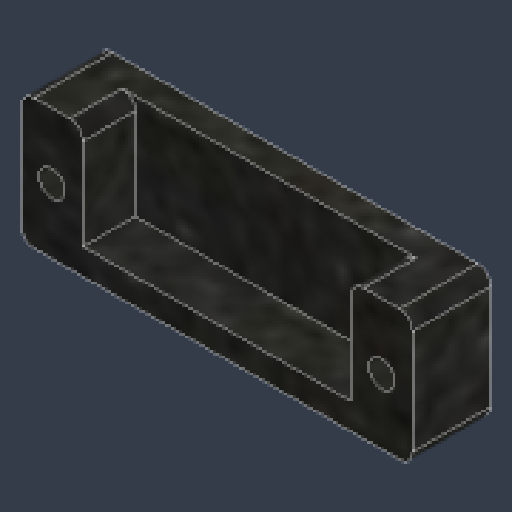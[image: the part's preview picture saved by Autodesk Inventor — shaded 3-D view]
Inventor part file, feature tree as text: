
AUTODESK INVENTOR PART (.ipt)
format: ipt  version: 2023.4 (Build 274418000, 418)  size: 148,480 bytes
history: native  units: mm
features: sketch x3, extrude x2, hole x1, fillet x1
ambient origin geometry x8: Origin, YZ Plane, XZ Plane, XY Plane, X Axis, Y Axis, Z Axis, Center Point
bodies: Solid1 (feature_tree)
feature tree (7):
  extrude  "Extrusion1"  Depth=20.0mm
  extrude  "Extrusion2"  Depth=41.0mm
  hole  "Hole1"  [1 undecoded]
  fillet  "Fillet1"  Radius=9.5mm
  sketch  "Sketch1"  dims[d0=60.0mm d1=20.0mm]
  sketch  "Sketch2"  dims[d2=12.0mm d3=0.0mm d4=41.0mm]
  sketch  "Sketch3"  dims[d5=4.0mm d6=8.0mm d7=0.0mm d8=9.5mm d9=4.75mm d10=4.0mm d11=6.0mm d12=7.5mm d13=2.0mm d14=90.0deg d15=8.0mm d16=20.594885mm d17=2.0mm]
note: 1 required parameter value undecoded (feature->parameter linkage not recoverable at this tier; creation-order binding heuristic only, values carry confidence <= 0.55)
